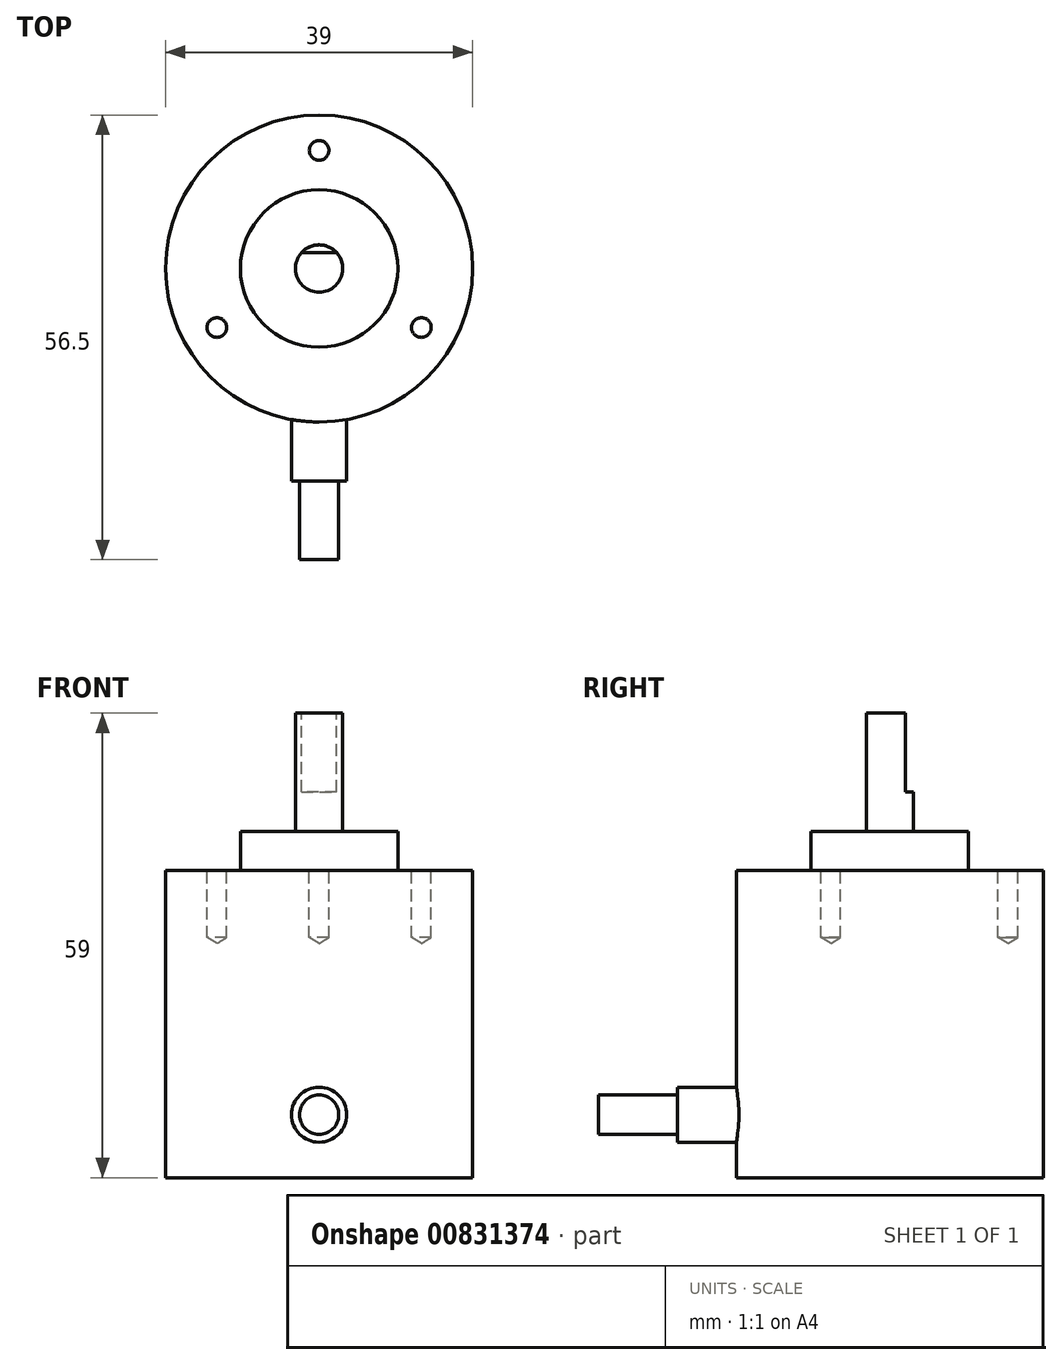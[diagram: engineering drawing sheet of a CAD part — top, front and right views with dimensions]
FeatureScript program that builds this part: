
annotation { "Feature Type Name" : "Feature", "Feature Type Description" : "" }
export const myFeature = defineFeature(function(context is Context, id is Id, definition is map)
    precondition{}
    {
        {
            var Q0;
            Q0=qCreatedBy(makeId("Top.planeOp"),FACE);
            var sketch = newSketch(context, id + "F0", { "sketchPlane" : qUnion([Q0])});
            skCircle(sketch, "E0", {"center": v(0, 0) * mm, "radius": 19.5 * mm});
            skSolve(sketch);
        }
        {
            var Q0;
            Q0 = qSketchRegion(id + "F0", true);
            extrude(context, id + "F1", {"entities" : qUnion([Q0]), "depth" : 39 * mm, "offsetDistance" : 25 * mm});
        }
        {
            var Q0;
            Q0=makeQuery(id+"F1.opExtrude","CAP_FACE",FACE,{"disambiguationData":[OSD([sQuery(id+"F0.wireOp",EDGE,"E0")])],"isStart":false});
            var sketch = newSketch(context, id + "F2", { "sketchPlane" : qUnion([Q0])});
            skCircle(sketch, "E1", {"center": v(0, 0) * mm, "radius": 10 * mm});
            skSolve(sketch);
        }
        {
            var Q0;
            Q0 = qSketchRegion(id + "F2", true);
            extrude(context, id + "F3", {"entities" : qUnion([Q0]), "operationType" : NewBodyOperationType.ADD, "depth" : 5 * mm, "offsetDistance" : 25 * mm});
        }
        {
            var Q0;
            Q0=makeQuery(id+"F3.opExtrude","CAP_FACE",FACE,{"disambiguationData":[OSD([sQuery(id+"F2.wireOp",EDGE,"E1")])],"isStart":false});
            var sketch = newSketch(context, id + "F4", { "sketchPlane" : qUnion([Q0])});
            skCircle(sketch, "E2", {"center": v(0, 0) * mm, "radius": 3 * mm});
            skSolve(sketch);
        }
        {
            var Q0;
            Q0 = qSketchRegion(id + "F4", true);
            extrude(context, id + "F5", {"entities" : qUnion([Q0]), "operationType" : NewBodyOperationType.ADD, "depth" : 15 * mm, "offsetDistance" : 25 * mm});
        }
        {
            var Q0;
            Q0=makeQuery(id+"F1.opExtrude","CAP_FACE",FACE,{"disambiguationData":[OSD([sQuery(id+"F0.wireOp",EDGE,"E0")])],"isStart":false});
            var sketch = newSketch(context, id + "F6", { "sketchPlane" : qUnion([Q0])});
            skCircle(sketch, "E3.cCircle", {"center": v(0, 0) * mm, "radius": 15 * mm, "construction": true});
            skLineSegment(sketch, "E3.0", {"start": v(0, 15) * mm, "end": v(13, -7.5) * mm});
            skLineSegment(sketch, "E3.1", {"start": v(13, -7.5) * mm, "end": v(-13, -7.5) * mm});
            skLineSegment(sketch, "E3.2", {"start": v(-13, -7.5) * mm, "end": v(0, 15) * mm});
            skLineSegment(sketch, "E4", {"start": v(0, 0) * mm, "end": v(0, 15) * mm, "construction": true});
            skSolve(sketch);
        }
        {
            var Q0;
            Q0=sQuery(id+"F6.wireOp",VERTEX,"E3.0.start");
            var Q1;
            Q1=sQuery(id+"F6.wireOp",VERTEX,"E3.1.end");
            var Q2;
            Q2=sQuery(id+"F6.wireOp",VERTEX,"E3.0.end");
            var Q3;
            Q3=makeQuery(id+"F1.opExtrude","SWEPT_BODY",BODY,{"disambiguationData":[OSD([sQuery(id+"F0.wireOp",EDGE,"E0")])]});
            hole(context, id + "F7", {"style" : HoleStyle.SIMPLE, "endStyle" : HoleEndStyle.BLIND, "standardTappedOrClearance" : lookupTablePath({ "standard" : "ISO", "engagement" : "75%", "pitch" : "0.5 mm", "size" : "M3", "type" : "Tapped" }), "standardBlindInLast" : lookupTablePath({ "standard" : "ISO", "engagement" : "75%", "pitch" : "0.5 mm", "size" : "M3", "type" : "Tapped" }), "holeDiameter" : 2.5 * mm, "majorDiameter" : 3 * mm, "showTappedDepth" : true, "holeDepth" : 8.5 * mm, "isTappedThrough" : true, "tappedDepth" : 7 * mm, "tapClearance" : 3, "startFromSketch" : true, "locations" : qUnion([Q0, Q1, Q2]), "scope" : qUnion([Q3])});
        }
        {
            var Q0;
            Q0=makeQuery(id+"F5.opExtrude","CAP_FACE",FACE,{"disambiguationData":[OSD([sQuery(id+"F4.wireOp",EDGE,"E2")])],"isStart":false});
            var sketch = newSketch(context, id + "F8", { "sketchPlane" : qUnion([Q0])});
            skLineSegment(sketch, "E5.bottom", {"start": v(-2.24, 2) * mm, "end": v(2.24, 2) * mm});
            skLineSegment(sketch, "E5.top", {"start": v(-2.24, 3) * mm, "end": v(2.24, 3) * mm});
            skLineSegment(sketch, "E5.left", {"start": v(-2.24, 2) * mm, "end": v(-2.24, 3) * mm});
            skLineSegment(sketch, "E5.right", {"start": v(2.24, 2) * mm, "end": v(2.24, 3) * mm});
            skSolve(sketch);
        }
        {
            var Q0;
            Q0 = qSketchRegion(id + "F8", true);
            extrude(context, id + "F9", {"entities" : qUnion([Q0]), "operationType" : NewBodyOperationType.REMOVE, "oppositeDirection" : true, "depth" : 10 * mm, "offsetDistance" : 25 * mm});
        }
        {
            var Q0;
            Q0=qCreatedBy(makeId("Front.planeOp"),FACE);
            var sketch = newSketch(context, id + "F10", { "sketchPlane" : qUnion([Q0])});
            skLineSegment(sketch, "E6", {"start": v(0, 0) * mm, "end": v(0, 8) * mm, "construction": true});
            skCircle(sketch, "E7", {"center": v(0, 8) * mm, "radius": 3.5 * mm});
            skSolve(sketch);
        }
        {
            var Q0;
            Q0 = qSketchRegion(id + "F10", true);
            extrude(context, id + "F11", {"entities" : qUnion([Q0]), "operationType" : NewBodyOperationType.ADD, "depth" : (39 / 2 + 7.5) * mm, "offsetDistance" : 25 * mm});
        }
        {
            var Q0;
            Q0=makeQuery(id+"F11.opExtrude","CAP_FACE",FACE,{"disambiguationData":[OSD([sQuery(id+"F10.wireOp",EDGE,"E7")])],"isStart":false});
            var sketch = newSketch(context, id + "F12", { "sketchPlane" : qUnion([Q0])});
            skCircle(sketch, "E8", {"center": v(0, 8) * mm, "radius": 2.5 * mm});
            skSolve(sketch);
        }
        {
            var Q0;
            Q0 = qSketchRegion(id + "F12", true);
            extrude(context, id + "F13", {"entities" : qUnion([Q0]), "operationType" : NewBodyOperationType.ADD, "depth" : 10 * mm, "offsetDistance" : 25 * mm});
        }
    });
